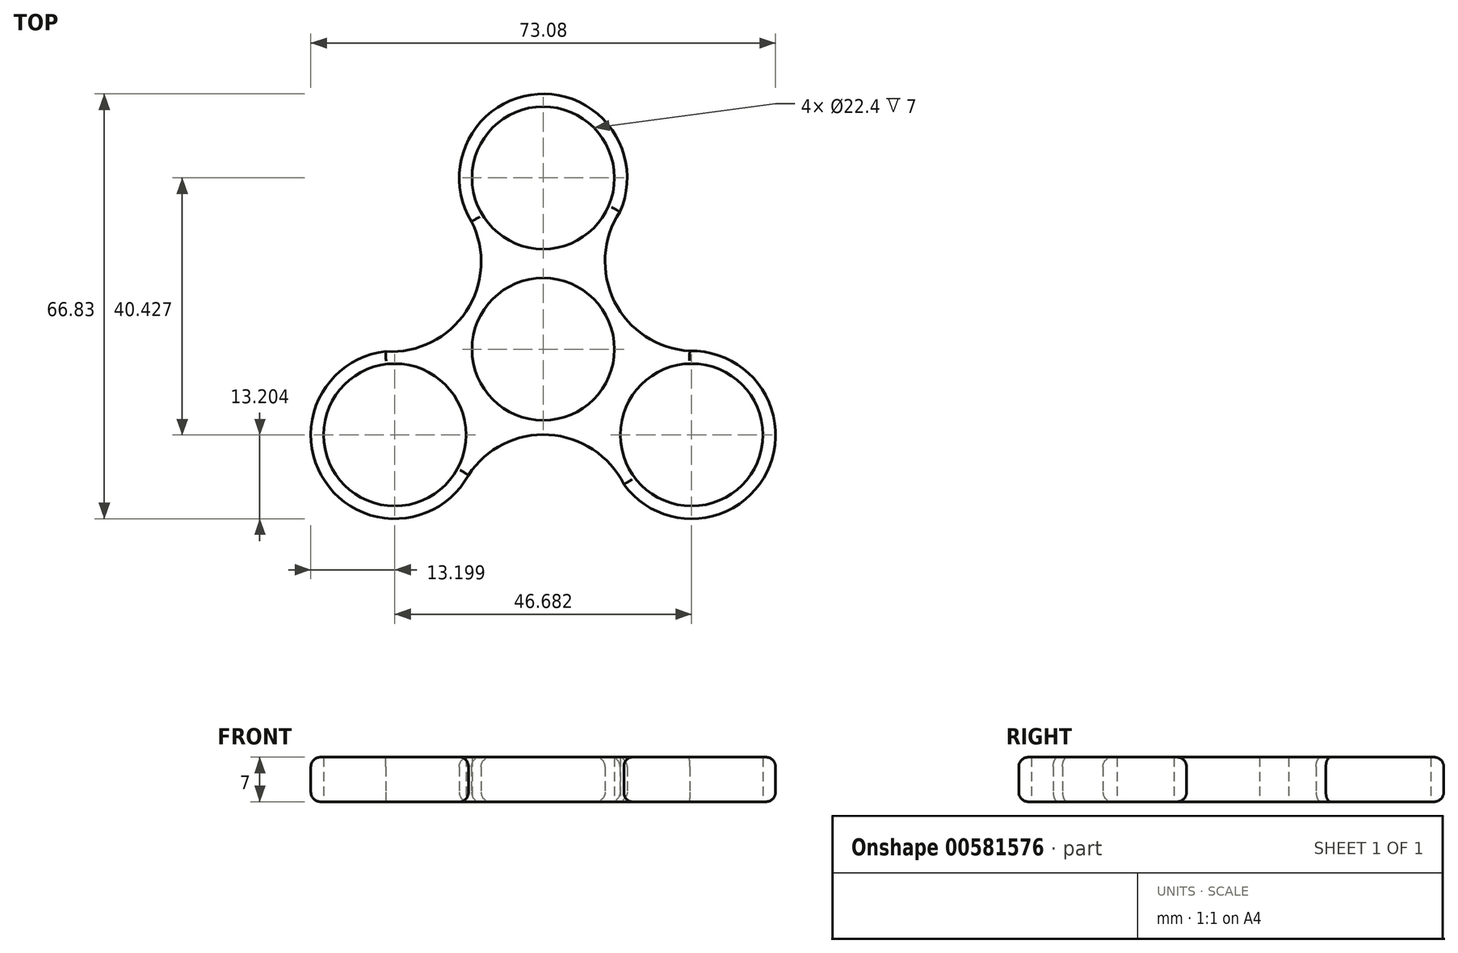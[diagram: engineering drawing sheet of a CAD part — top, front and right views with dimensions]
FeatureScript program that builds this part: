
annotation { "Feature Type Name" : "Feature", "Feature Type Description" : "" }
export const myFeature = defineFeature(function(context is Context, id is Id, definition is map)
    precondition{}
    {
        {
            var Q0;
            Q0=qCreatedBy(makeId("Top.planeOp"),FACE);
            var sketch = newSketch(context, id + "F0", { "sketchPlane" : qUnion([Q0])});
            skCircle(sketch, "E0", {"center": v(0, 0) * mm, "radius": 11.2 * mm});
            skCircle(sketch, "E1", {"center": v(0, 26.95) * mm, "radius": 11.2 * mm});
            skArc(sketch, "E2", {"start": v(10.96, 19.6) * mm, "mid": v(0.3, 40.15) * mm, "end": v(-11.27, 20.08) * mm});
            skArc(sketch, "E3.1.0", {"start": v(-22.44, -0.3) * mm, "mid": v(-34.92, -19.82) * mm, "end": v(-11.76, -19.8) * mm});
            skCircle(sketch, "E3.1.1", {"center": v(-23.34, -13.48) * mm, "radius": 11.2 * mm});
            skArc(sketch, "E3.2.0", {"start": v(11.49, -19.28) * mm, "mid": v(34.62, -20.33) * mm, "end": v(23.03, -0.28) * mm});
            skCircle(sketch, "E3.2.1", {"center": v(23.34, -13.48) * mm, "radius": 11.2 * mm});
            skArc(sketch, "E4", {"start": v(12.08, 21.62) * mm, "mid": v(11.21, 7.5) * mm, "end": v(23.03, -0.28) * mm});
            skArc(sketch, "E5.1.0", {"start": v(-24.76, -0.35) * mm, "mid": v(-12.1, 5.96) * mm, "end": v(-11.27, 20.08) * mm});
            skArc(sketch, "E5.2.0", {"start": v(12.69, -21.27) * mm, "mid": v(0.89, -13.46) * mm, "end": v(-11.76, -19.8) * mm});
            skSolve(sketch);
        }
        {
            var Q0;
            Q0=makeQuery(id+"F0.imprint","IMPRINT",FACE,{"disambiguationData":[TD([[makeQuery(id+"F0.imprint","IMPRINT",EDGE,{"derivedFrom":sQuery(id+"F0.wireOp",EDGE,"E0")}),-1.0]])]});
            extrude(context, id + "F1", {"entities" : qUnion([Q0]), "depth" : 7 * mm, "offsetDistance" : 25 * mm});
        }
        {
            var Q0;
            Q0=makeQuery(id+"F1.opExtrude","CAP_EDGE",EDGE,{"disambiguationData":[OSD([sQuery(id+"F0.wireOp",EDGE,"E5.2.0")])],"isStart":false});
            var Q1;
            Q1=makeQuery(id+"F1.opExtrude","CAP_EDGE",EDGE,{"disambiguationData":[OSD([sQuery(id+"F0.wireOp",EDGE,"E3.1.0")])],"isStart":false});
            var Q2;
            Q2=makeQuery(id+"F1.opExtrude","CAP_EDGE",EDGE,{"disambiguationData":[OSD([sQuery(id+"F0.wireOp",EDGE,"E5.1.0")])],"isStart":false});
            var Q3;
            Q3=makeQuery(id+"F1.opExtrude","CAP_EDGE",EDGE,{"disambiguationData":[OSD([sQuery(id+"F0.wireOp",EDGE,"E2")])],"isStart":false});
            var Q4;
            Q4=makeQuery(id+"F1.opExtrude","CAP_EDGE",EDGE,{"disambiguationData":[OSD([sQuery(id+"F0.wireOp",EDGE,"E4")])],"isStart":false});
            var Q5;
            Q5=makeQuery(id+"F1.opExtrude","CAP_EDGE",EDGE,{"disambiguationData":[OSD([sQuery(id+"F0.wireOp",EDGE,"E3.2.0")])],"isStart":false});
            fillet(context, id + "F2", {"entities" : qUnion([Q0, Q1, Q2, Q3, Q4, Q5]), "radius" : 1.5 * mm, "tangentPropagation" : true, "allowEdgeOverflow" : false});
        }
        {
            var Q0;
            Q0=makeQuery(id+"F1.opExtrude","CAP_EDGE",EDGE,{"disambiguationData":[OSD([sQuery(id+"F0.wireOp",EDGE,"E3.1.0")])],"isStart":true});
            var Q1;
            Q1=makeQuery(id+"F1.opExtrude","CAP_EDGE",EDGE,{"disambiguationData":[OSD([sQuery(id+"F0.wireOp",EDGE,"E5.1.0")])],"isStart":true});
            var Q2;
            Q2=makeQuery(id+"F1.opExtrude","CAP_EDGE",EDGE,{"disambiguationData":[OSD([sQuery(id+"F0.wireOp",EDGE,"E2")])],"isStart":true});
            var Q3;
            Q3=makeQuery(id+"F1.opExtrude","CAP_EDGE",EDGE,{"disambiguationData":[OSD([sQuery(id+"F0.wireOp",EDGE,"E4")])],"isStart":true});
            var Q4;
            Q4=makeQuery(id+"F1.opExtrude","CAP_EDGE",EDGE,{"disambiguationData":[OSD([sQuery(id+"F0.wireOp",EDGE,"E3.2.0")])],"isStart":true});
            fillet(context, id + "F3", {"entities" : qUnion([Q0, Q1, Q2, Q3, Q4]), "radius" : 1.5 * mm, "tangentPropagation" : true, "allowEdgeOverflow" : false});
        }
    });
